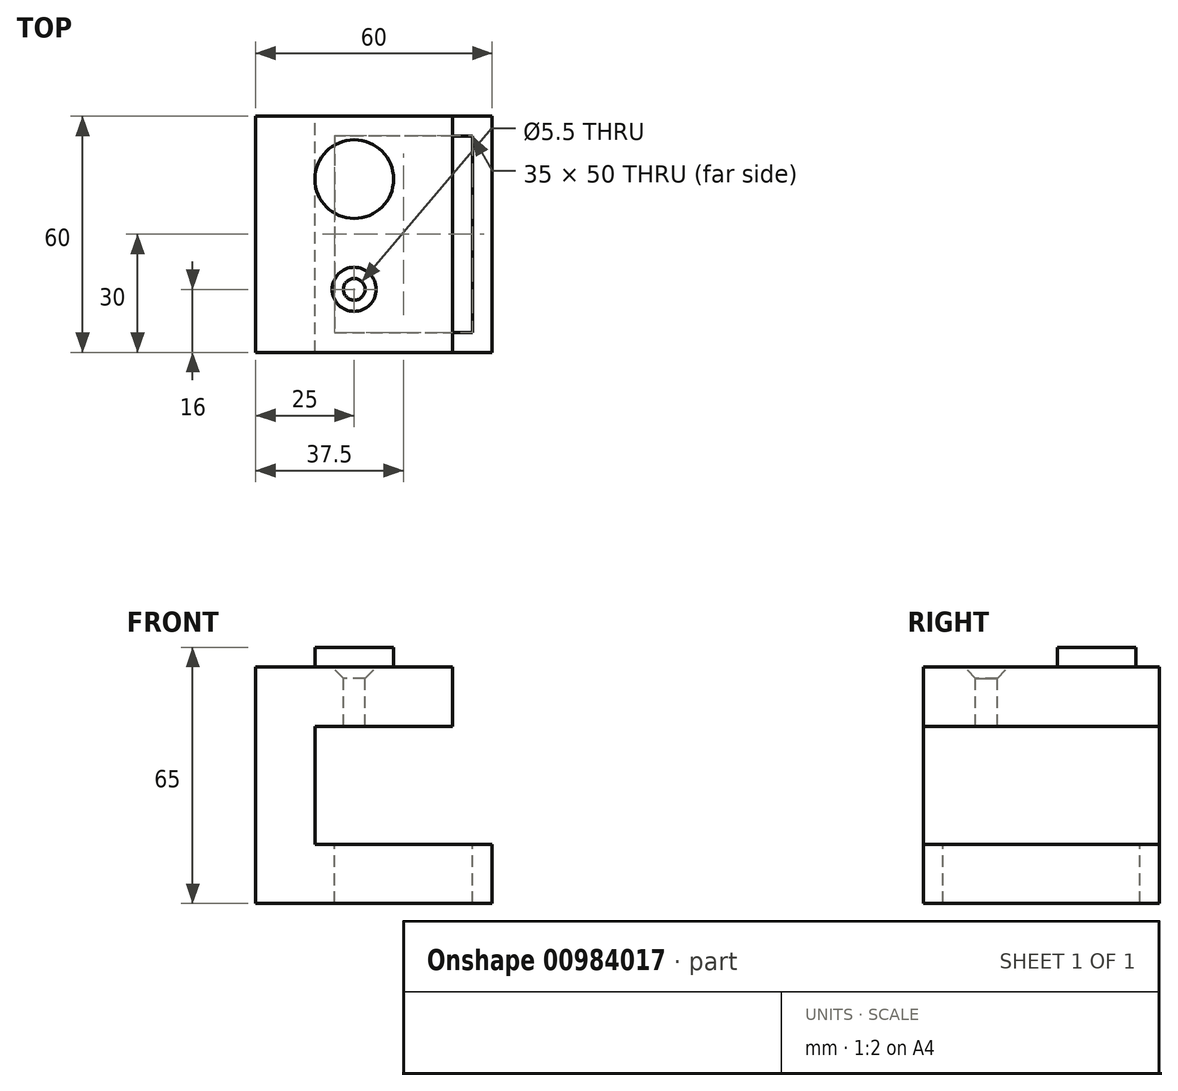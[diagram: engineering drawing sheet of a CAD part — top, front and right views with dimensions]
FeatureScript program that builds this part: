
annotation { "Feature Type Name" : "Feature", "Feature Type Description" : "" }
export const myFeature = defineFeature(function(context is Context, id is Id, definition is map)
    precondition{}
    {
        {
            var Q0;
            Q0=qCreatedBy(makeId("Front.planeOp"),FACE);
            var sketch = newSketch(context, id + "F0", { "sketchPlane" : qUnion([Q0])});
            skLineSegment(sketch, "E0", {"start": v(50, 60) * mm, "end": v(0, 60) * mm});
            skLineSegment(sketch, "E1", {"start": v(0, 60) * mm, "end": v(0, 0) * mm});
            skLineSegment(sketch, "E2", {"start": v(0, 0) * mm, "end": v(60, 0) * mm});
            skLineSegment(sketch, "E3", {"start": v(60, 0) * mm, "end": v(60, 15) * mm});
            skLineSegment(sketch, "E4", {"start": v(60, 15) * mm, "end": v(15, 15) * mm});
            skLineSegment(sketch, "E5", {"start": v(15, 15) * mm, "end": v(15, 45) * mm});
            skLineSegment(sketch, "E6", {"start": v(15, 45) * mm, "end": v(50, 45) * mm});
            skLineSegment(sketch, "E7", {"start": v(50, 45) * mm, "end": v(50, 60) * mm});
            skSolve(sketch);
        }
        {
            var Q0;
            Q0=makeQuery(id+"F0.imprint","IMPRINT",FACE,{"disambiguationData":[TD([[makeQuery(id+"F0.imprint","IMPRINT",EDGE,{"derivedFrom":sQuery(id+"F0.wireOp",EDGE,"E0")}),1.0]])]});
            extrude(context, id + "F1", {"entities" : qUnion([Q0]), "endBound" : BoundingType.SYMMETRIC, "depth" : 60 * mm, "offsetDistance" : 25 * mm});
        }
        {
            var Q0;
            Q0=makeQuery(id+"F1.opExtrude","SWEPT_FACE",FACE,{"disambiguationData":[OSD([sQuery(id+"F0.wireOp",EDGE,"E4")])]});
            var sketch = newSketch(context, id + "F2", { "sketchPlane" : qUnion([Q0])});
            skLineSegment(sketch, "E8.0", {"start": v(55, 25) * mm, "end": v(20, 25) * mm});
            skLineSegment(sketch, "E8.1", {"start": v(55, -25) * mm, "end": v(55, 25) * mm});
            skLineSegment(sketch, "E8.2", {"start": v(20, -25) * mm, "end": v(55, -25) * mm});
            skLineSegment(sketch, "E8.3", {"start": v(20, 25) * mm, "end": v(20, -25) * mm});
            skSolve(sketch);
        }
        {
            var Q0;
            Q0=makeQuery(id+"F2.imprint","IMPRINT",FACE,{"disambiguationData":[TD([[makeQuery(id+"F2.imprint","IMPRINT",EDGE,{"derivedFrom":sQuery(id+"F2.wireOp",EDGE,"E8.0")}),1.0]])]});
            extrude(context, id + "F3", {"entities" : qUnion([Q0]), "operationType" : NewBodyOperationType.REMOVE, "endBound" : BoundingType.THROUGH_ALL, "oppositeDirection" : true, "depth" : 25 * mm, "offsetDistance" : 25 * mm});
        }
        {
            var Q0;
            Q0=makeQuery(id+"F1.opExtrude","SWEPT_FACE",FACE,{"disambiguationData":[OSD([sQuery(id+"F0.wireOp",EDGE,"E0")])]});
            var sketch = newSketch(context, id + "F4", { "sketchPlane" : qUnion([Q0])});
            skCircle(sketch, "E9", {"center": v(25, 14) * mm, "radius": 10 * mm});
            skPoint(sketch, "E10", {"position": v(25, -14) * mm});
            skSolve(sketch);
        }
        {
            var Q0;
            Q0=sQuery(id+"F4.wireOp",VERTEX,"E10");
            var Q1;
            Q1=makeQuery(id+"F1.opExtrude","SWEPT_BODY",BODY,{"disambiguationData":[OSD([sQuery(id+"F0.wireOp",EDGE,"E0"),sQuery(id+"F0.wireOp",EDGE,"E1"),sQuery(id+"F0.wireOp",EDGE,"E2"),sQuery(id+"F0.wireOp",EDGE,"E3"),sQuery(id+"F0.wireOp",EDGE,"E4"),sQuery(id+"F0.wireOp",EDGE,"E5"),sQuery(id+"F0.wireOp",EDGE,"E6"),sQuery(id+"F0.wireOp",EDGE,"E7")])]});
            hole(context, id + "F5", {"style" : HoleStyle.C_SINK, "endStyle" : HoleEndStyle.THROUGH, "standardTappedOrClearance" : lookupTablePath({ "fit" : "Normal", "standard" : "ISO", "size" : "M5", "type" : "Clearance" }), "standardBlindInLast" : lookupTablePath({ "fit" : "Normal", "standard" : "ISO", "engagement" : "75%", "pitch" : "0.8 mm", "size" : "M5", "type" : "Clearance & tapped" }), "holeDiameter" : 5.5 * mm, "cSinkDiameter" : 11.2 * mm, "cSinkAngle" : 90 * degree, "majorDiameter" : 5 * mm, "isTappedThrough" : true, "tappedDepth" : 12 * mm, "tapClearance" : 3, "locations" : qUnion([Q0]), "scope" : qUnion([Q1])});
        }
        {
            var Q0;
            Q0=makeQuery(id+"F4.imprint","IMPRINT",FACE,{"disambiguationData":[TD([[makeQuery(id+"F4.imprint","IMPRINT",EDGE,{"derivedFrom":sQuery(id+"F4.wireOp",EDGE,"E9")}),1.0]])]});
            var Q1;
            Q1=sQuery(id+"F4.wireOp",EDGE,"E9");
            extrude(context, id + "F6", {"entities" : qUnion([Q0]), "operationType" : NewBodyOperationType.ADD, "surfaceOperationType" : NewSurfaceOperationType.ADD, "surfaceEntities" : qUnion([Q1]), "depth" : 5 * mm, "offsetDistance" : 25 * mm});
        }
        {
            var Q0;
            Q0=makeQuery(id+"F6.opExtrude","CAP_FACE",FACE,{"disambiguationData":[OSD([sQuery(id+"F4.wireOp",EDGE,"E9")])],"isStart":false});
            var sketch = newSketch(context, id + "F7", { "sketchPlane" : qUnion([Q0])});
            skCircle(sketch, "E11", {"center": v(25, 14) * mm, "radius": 8.32 * mm});
            skSolve(sketch);
        }
        {
            var Q0;
            Q0 = qSketchRegion(id + "F7", true);
            extrude(context, id + "F8", {"entities" : qUnion([Q0]), "operationType" : NewBodyOperationType.ADD, "depth" : -5 * mm, "offsetDistance" : 25 * mm});
        }
    });
